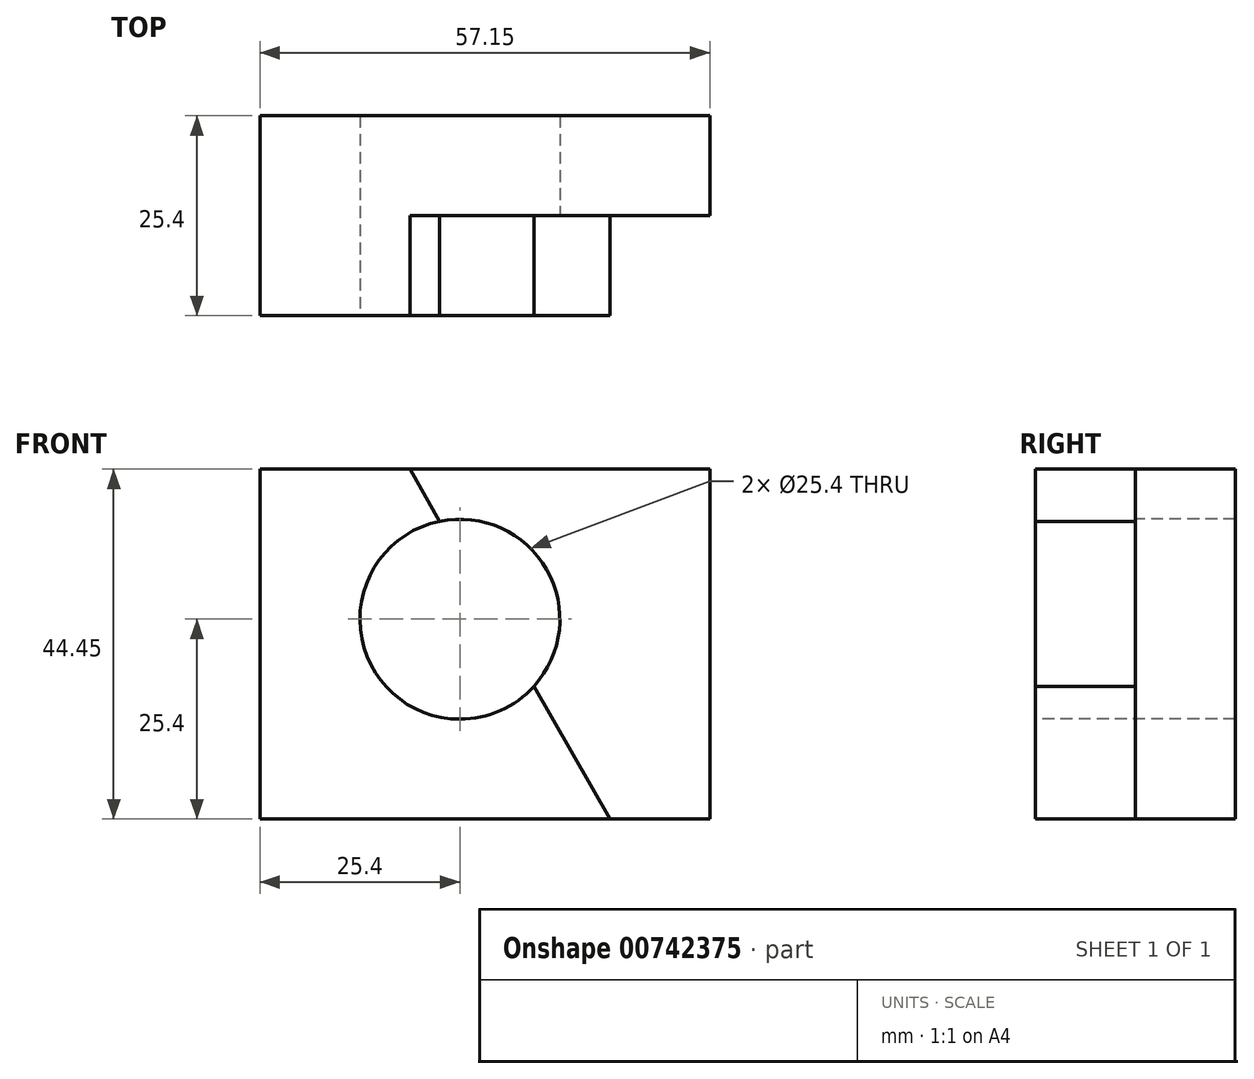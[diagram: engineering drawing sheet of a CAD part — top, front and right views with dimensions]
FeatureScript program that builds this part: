
annotation { "Feature Type Name" : "Feature", "Feature Type Description" : "" }
export const myFeature = defineFeature(function(context is Context, id is Id, definition is map)
    precondition{}
    {
        {
            var Q0;
            Q0=qCreatedBy(makeId("Front.planeOp"),FACE);
            var sketch = newSketch(context, id + "F0", { "sketchPlane" : qUnion([Q0])});
            skLineSegment(sketch, "E0.bottom", {"start": v(0, 0) * mm, "end": v(-57.15, 0) * mm});
            skLineSegment(sketch, "E0.top", {"start": v(0, 44.45) * mm, "end": v(-57.15, 44.45) * mm});
            skLineSegment(sketch, "E0.left", {"start": v(0, 0) * mm, "end": v(0, 44.45) * mm});
            skLineSegment(sketch, "E0.right", {"start": v(-57.15, 0) * mm, "end": v(-57.15, 44.45) * mm});
            skSolve(sketch);
        }
        {
            var Q0;
            Q0=makeQuery(id+"F0.imprint","IMPRINT",FACE,{"disambiguationData":[TD([[makeQuery(id+"F0.imprint","IMPRINT",EDGE,{"derivedFrom":sQuery(id+"F0.wireOp",EDGE,"E0.bottom")}),-1.0]])]});
            extrude(context, id + "F1", {"entities" : qUnion([Q0]), "depth" : 25.4 * mm, "offsetDistance" : 25.4 * mm});
        }
        {
            var Q0;
            Q0=makeQuery(id+"F1.opExtrude","CAP_FACE",FACE,{"disambiguationData":[OSD([sQuery(id+"F0.wireOp",EDGE,"E0.bottom"),sQuery(id+"F0.wireOp",EDGE,"E0.top"),sQuery(id+"F0.wireOp",EDGE,"E0.left"),sQuery(id+"F0.wireOp",EDGE,"E0.right")])],"isStart":false});
            var sketch = newSketch(context, id + "F2", { "sketchPlane" : qUnion([Q0])});
            skCircle(sketch, "E1", {"center": v(-31.75, 25.4) * mm, "radius": 12.7 * mm});
            skSolve(sketch);
        }
        {
            var Q0;
            Q0=makeQuery(id+"F2.imprint","IMPRINT",FACE,{"disambiguationData":[TD([[makeQuery(id+"F2.imprint","IMPRINT",EDGE,{"derivedFrom":sQuery(id+"F2.wireOp",EDGE,"E1")}),1.0]])]});
            extrude(context, id + "F3", {"entities" : qUnion([Q0]), "operationType" : NewBodyOperationType.REMOVE, "endBound" : BoundingType.THROUGH_ALL, "oppositeDirection" : true, "depth" : 25.4 * mm, "offsetDistance" : 25.4 * mm});
        }
        {
            var Q0;
            Q0=makeQuery(id+"F1.opExtrude","CAP_FACE",FACE,{"disambiguationData":[OSD([sQuery(id+"F0.wireOp",EDGE,"E0.bottom"),sQuery(id+"F0.wireOp",EDGE,"E0.top"),sQuery(id+"F0.wireOp",EDGE,"E0.left"),sQuery(id+"F0.wireOp",EDGE,"E0.right")])],"isStart":false});
            var sketch = newSketch(context, id + "F4", { "sketchPlane" : qUnion([Q0])});
            skLineSegment(sketch, "E2", {"start": v(-38.1, 44.45) * mm, "end": v(-12.7, 0) * mm});
            skSolve(sketch);
        }
        {
            var Q0;
            {var subQ0=makeQuery(id+"F1.opExtrude","CAP_EDGE",EDGE,{"disambiguationData":[OSD([sQuery(id+"F0.wireOp",EDGE,"E0.left")])],"isStart":false});Q0=makeQuery(id+"F4.imprint","IMPRINT",FACE,{"disambiguationData":[TD([[makeQuery(id+"F4.imprint","IMPRINT",EDGE,{"derivedFrom":subQ0}),1.0]])]});}
            extrude(context, id + "F5", {"entities" : qUnion([Q0]), "operationType" : NewBodyOperationType.REMOVE, "oppositeDirection" : true, "depth" : 12.7 * mm, "offsetDistance" : 25.4 * mm});
        }
    });
